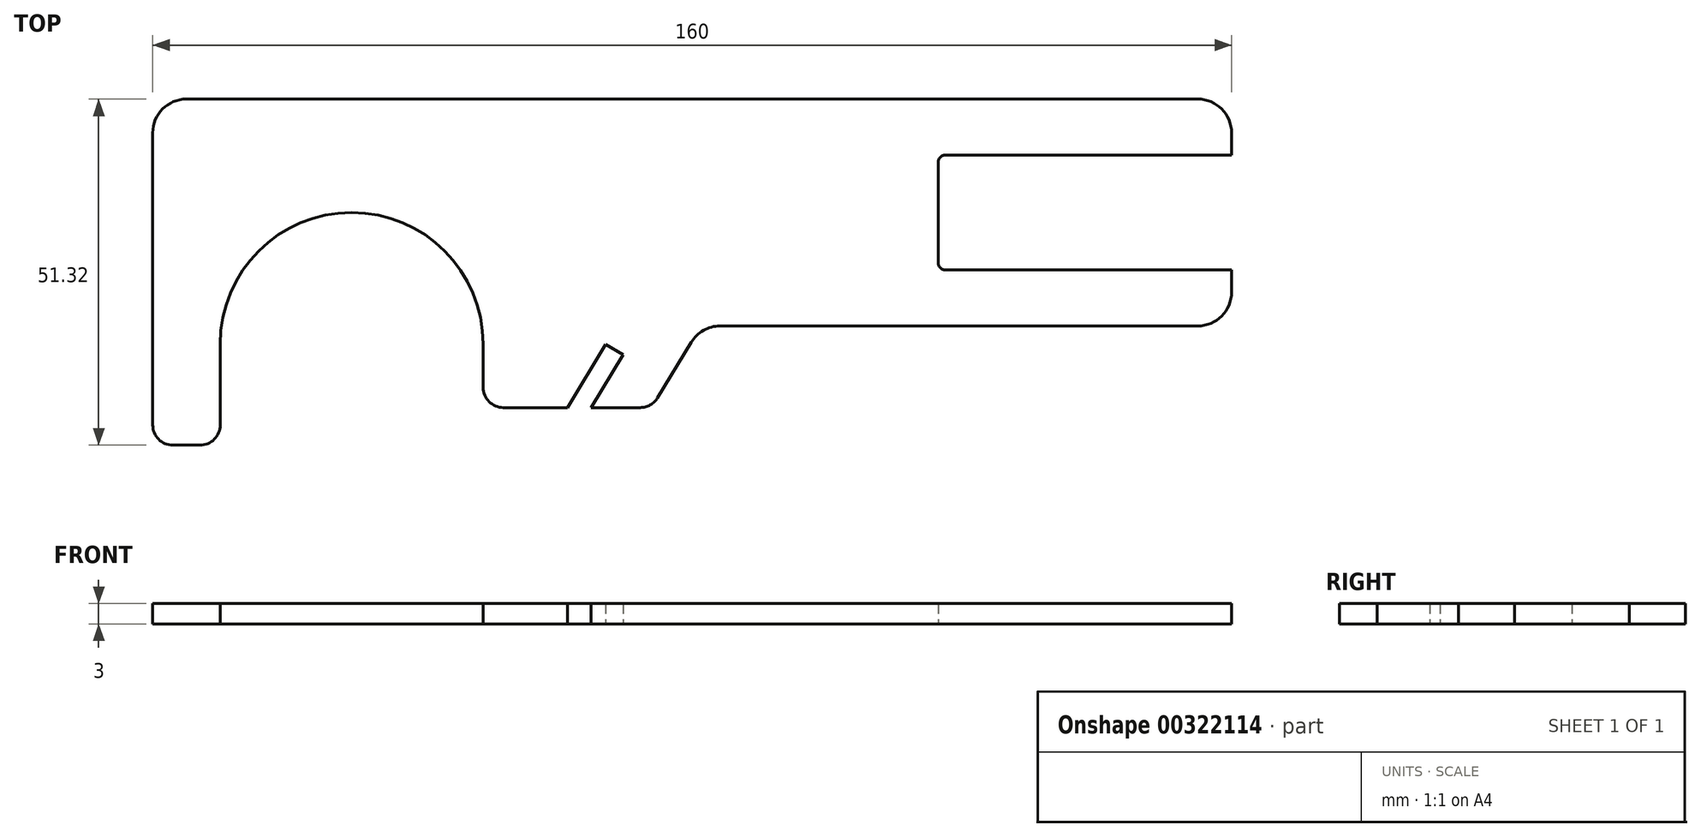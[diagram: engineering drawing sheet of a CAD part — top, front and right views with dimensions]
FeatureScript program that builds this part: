
annotation { "Feature Type Name" : "Feature", "Feature Type Description" : "" }
export const myFeature = defineFeature(function(context is Context, id is Id, definition is map)
    precondition{}
    {
        {
            var Q0;
            Q0=qCreatedBy(makeId("Top.planeOp"),FACE);
            var sketch = newSketch(context, id + "F0", { "sketchPlane" : qUnion([Q0])});
            skArc(sketch, "E0", {"start": v(19.5, 0) * mm, "mid": v(0, 19.5) * mm, "end": v(-19.5, 0) * mm});
            skLineSegment(sketch, "E1", {"start": v(-19.5, 0) * mm, "end": v(-19.5, 19.5) * mm, "construction": true});
            skLineSegment(sketch, "E2", {"start": v(-19.5, 19.5) * mm, "end": v(119, 19.5) * mm, "construction": true});
            skLineSegment(sketch, "E3", {"start": v(-19.5, 0) * mm, "end": v(-19.5, -15) * mm, "construction": true});
            skLineSegment(sketch, "E4", {"start": v(-19.5, -15) * mm, "end": v(-29.5, -15) * mm, "construction": true});
            skLineSegment(sketch, "E5.bottom", {"start": v(-26.5, -15) * mm, "end": v(-22.5, -15) * mm});
            skLineSegment(sketch, "E5.left", {"start": v(-29.5, -12) * mm, "end": v(-29.5, 21.5) * mm});
            skLineSegment(sketch, "E6", {"start": v(-10.5, -19.5) * mm, "end": v(10.5, -19.5) * mm, "construction": true});
            skPoint(sketch, "E7", {"position": v(0, -19.5) * mm});
            skLineSegment(sketch, "E8", {"start": v(0, 0) * mm, "end": v(0, -19.5) * mm, "construction": true});
            skLineSegment(sketch, "E9", {"start": v(-35, -74.5) * mm, "end": v(35, -74.5) * mm, "construction": true});
            skPoint(sketch, "E10", {"position": v(0, -74.5) * mm});
            skLineSegment(sketch, "E11", {"start": v(0, -19.5) * mm, "end": v(0, -74.5) * mm, "construction": true});
            skLineSegment(sketch, "E12", {"start": v(10.5, -19.5) * mm, "end": v(35, -74.5) * mm, "construction": true});
            skLineSegment(sketch, "E13", {"start": v(-10.5, -19.5) * mm, "end": v(-35, -74.5) * mm, "construction": true});
            skLineSegment(sketch, "E14", {"start": v(19.5, 0) * mm, "end": v(19.5, -6.43) * mm});
            skLineSegment(sketch, "E15", {"start": v(32.02, -9.43) * mm, "end": v(37.7, -0.05) * mm});
            skLineSegment(sketch, "E16", {"start": v(37.7, -0.05) * mm, "end": v(40.26, -1.6) * mm});
            skLineSegment(sketch, "E17", {"start": v(40.26, -1.6) * mm, "end": v(35.53, -9.43) * mm});
            skLineSegment(sketch, "E18", {"start": v(22.5, -9.43) * mm, "end": v(32, -9.43) * mm});
            skLineSegment(sketch, "E19", {"start": v(45.38, -7.98) * mm, "end": v(50.36, 0.26) * mm});
            skPoint(sketch, "E20.visualSharp", {"position": v(54.74, 7.5) * mm});
            skLineSegment(sketch, "E21", {"start": v(33.86, -9.43) * mm, "end": v(39.04, -0.87) * mm, "construction": true});
            skLineSegment(sketch, "E22", {"start": v(-19.5, -12) * mm, "end": v(-19.5, 0) * mm});
            skLineSegment(sketch, "E23", {"start": v(32, -9.43) * mm, "end": v(32.02, -9.43) * mm});
            skLineSegment(sketch, "E24.trimOffspring", {"start": v(35.53, -9.43) * mm, "end": v(42.8, -9.43) * mm});
            skPoint(sketch, "E25.visualSharp", {"position": v(-29.5, 31.5) * mm});
            skPoint(sketch, "E26.visualSharp", {"position": v(130.5, 31.5) * mm});
            skPoint(sketch, "E27.visualSharp", {"position": v(130.5, 7.5) * mm});
            skPoint(sketch, "E28.visualSharp", {"position": v(-19.5, -15) * mm});
            skArc(sketch, "E28.filletArc", {"start": v(-22.5, -15) * mm, "mid": v(-20.38, -14.12) * mm, "end": v(-19.5, -12) * mm});
            skPoint(sketch, "E29.visualSharp", {"position": v(-29.5, -15) * mm});
            skArc(sketch, "E29.filletArc", {"start": v(-29.5, -12) * mm, "mid": v(-28.62, -14.12) * mm, "end": v(-26.5, -15) * mm});
            skPoint(sketch, "E30.visualSharp", {"position": v(19.5, -9.43) * mm});
            skArc(sketch, "E30.filletArc", {"start": v(19.5, -6.43) * mm, "mid": v(20.38, -8.55) * mm, "end": v(22.5, -9.43) * mm});
            skPoint(sketch, "E31.visualSharp", {"position": v(44.5, -9.43) * mm});
            skArc(sketch, "E31.filletArc", {"start": v(42.8, -9.43) * mm, "mid": v(44.28, -9.04) * mm, "end": v(45.38, -7.98) * mm});
            skLineSegment(sketch, "E32", {"start": v(119, 19.5) * mm, "end": v(103, 19.5) * mm, "construction": true});
            skLineSegment(sketch, "E33.bottom", {"start": v(119, 28) * mm, "end": v(88, 28) * mm});
            skLineSegment(sketch, "E33.top", {"start": v(119, 11) * mm, "end": v(88, 11) * mm});
            skLineSegment(sketch, "E33.right", {"start": v(87, 27) * mm, "end": v(87, 12) * mm});
            skPoint(sketch, "E33.middle", {"position": v(103, 19.5) * mm});
            skLineSegment(sketch, "E34", {"start": v(54.64, 2.68) * mm, "end": v(125.5, 2.68) * mm});
            skLineSegment(sketch, "E35", {"start": v(130.5, 7.68) * mm, "end": v(130.5, 11) * mm});
            skLineSegment(sketch, "E36", {"start": v(130.5, 28) * mm, "end": v(130.5, 31.32) * mm});
            skLineSegment(sketch, "E37", {"start": v(125.5, 36.32) * mm, "end": v(-24.5, 36.32) * mm});
            skLineSegment(sketch, "E38", {"start": v(-29.5, 31.32) * mm, "end": v(-29.5, 21.5) * mm});
            skPoint(sketch, "E39.visualSharp", {"position": v(130.5, 36.32) * mm});
            skArc(sketch, "E39.filletArc", {"start": v(130.5, 31.32) * mm, "mid": v(129.04, 34.86) * mm, "end": v(125.5, 36.32) * mm});
            skPoint(sketch, "E40.visualSharp", {"position": v(130.5, 2.68) * mm});
            skArc(sketch, "E40.filletArc", {"start": v(125.5, 2.68) * mm, "mid": v(129.04, 4.14) * mm, "end": v(130.5, 7.68) * mm});
            skPoint(sketch, "E41.visualSharp", {"position": v(-29.5, 36.32) * mm});
            skArc(sketch, "E41.filletArc", {"start": v(-24.5, 36.32) * mm, "mid": v(-28.04, 34.86) * mm, "end": v(-29.5, 31.32) * mm});
            skLineSegment(sketch, "E42", {"start": v(119, 28) * mm, "end": v(130.5, 28) * mm});
            skLineSegment(sketch, "E43", {"start": v(119, 11) * mm, "end": v(130.5, 11) * mm});
            skLineSegment(sketch, "E44.trimOffspring", {"start": v(130.5, 11) * mm, "end": v(130.5, 7.5) * mm, "construction": true});
            skLineSegment(sketch, "E45.trimOffspring", {"start": v(130.5, 28) * mm, "end": v(130.5, 31.5) * mm, "construction": true});
            skPoint(sketch, "E46.visualSharp", {"position": v(51.82, 2.68) * mm});
            skArc(sketch, "E46.filletArc", {"start": v(54.64, 2.68) * mm, "mid": v(52.19, 2.03) * mm, "end": v(50.36, 0.26) * mm});
            skPoint(sketch, "E47.visualSharp", {"position": v(87, 28) * mm});
            skArc(sketch, "E47.filletArc", {"start": v(88, 28) * mm, "mid": v(87.3, 27.7) * mm, "end": v(87, 27) * mm});
            skPoint(sketch, "E48.visualSharp", {"position": v(87, 11) * mm});
            skArc(sketch, "E48.filletArc", {"start": v(87, 12) * mm, "mid": v(87.3, 11.3) * mm, "end": v(88, 11) * mm});
            skSolve(sketch);
        }
        {
            var Q0;
            Q0=makeQuery(id+"F0.imprint","IMPRINT",FACE,{"disambiguationData":[TD([[makeQuery(id+"F0.imprint","IMPRINT",EDGE,{"derivedFrom":sQuery(id+"F0.wireOp",EDGE,"E0")}),-1.0]])]});
            extrude(context, id + "F1", {"entities" : qUnion([Q0]), "depth" : 3 * mm});
        }
    });
